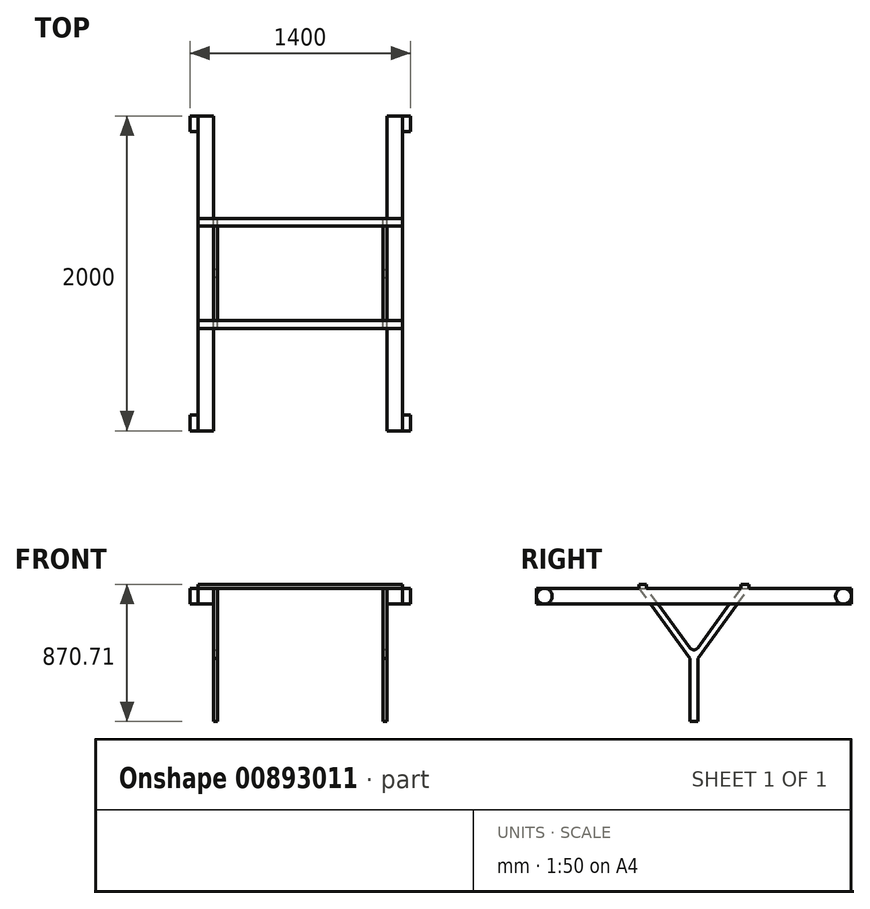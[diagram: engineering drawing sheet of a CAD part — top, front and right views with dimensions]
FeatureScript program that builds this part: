
annotation { "Feature Type Name" : "Feature", "Feature Type Description" : "" }
export const myFeature = defineFeature(function(context is Context, id is Id, definition is map)
    precondition{}
    {
        {
            var Q0;
            Q0=qCreatedBy(makeId("Top.planeOp"),FACE);
            var sketch = newSketch(context, id + "F0", { "sketchPlane" : qUnion([Q0])});
            skLineSegment(sketch, "E0.bottom", {"start": v(650, -1000) * mm, "end": v(550, -1000) * mm});
            skLineSegment(sketch, "E0.top", {"start": v(650, 1000) * mm, "end": v(550, 1000) * mm});
            skLineSegment(sketch, "E0.left", {"start": v(650, -1000) * mm, "end": v(650, 1000) * mm});
            skLineSegment(sketch, "E0.right", {"start": v(-650, -1000) * mm, "end": v(-650, 1000) * mm});
            skPoint(sketch, "E0.middle", {"position": v(0, 0) * mm});
            skLineSegment(sketch, "E1.left", {"start": v(-550, -1000) * mm, "end": v(-550, 1000) * mm});
            skLineSegment(sketch, "E1.right", {"start": v(550, -1000) * mm, "end": v(550, 1000) * mm});
            skLineSegment(sketch, "E2.trimOffspring", {"start": v(-550, 1000) * mm, "end": v(-650, 1000) * mm});
            skLineSegment(sketch, "E3.trimOffspring", {"start": v(-550, -1000) * mm, "end": v(-650, -1000) * mm});
            skSolve(sketch);
        }
        {
            var Q0;
            Q0=qSketchRegion(id+"F0",true);
            extrude(context, id + "F1", {"entities" : qUnion([Q0]), "depth" : 100 * mm, "offsetDistance" : 25 * mm});
        }
        {
            var Q0;
            Q0=makeQuery(id+"F1.opExtrude","CAP_FACE",FACE,{"disambiguationData":[OSD([sQuery(id+"F0.wireOp",EDGE,"E0.bottom"),sQuery(id+"F0.wireOp",EDGE,"E0.top"),sQuery(id+"F0.wireOp",EDGE,"E0.left"),sQuery(id+"F0.wireOp",EDGE,"E1.right")])],"isStart":false});
            var sketch = newSketch(context, id + "F2", { "sketchPlane" : qUnion([Q0])});
            skLineSegment(sketch, "E4.bottom", {"start": v(650, -350) * mm, "end": v(-650, -350) * mm});
            skLineSegment(sketch, "E4.top", {"start": v(650, -300) * mm, "end": v(-650, -300) * mm});
            skLineSegment(sketch, "E4.left", {"start": v(650, -350) * mm, "end": v(650, -300) * mm});
            skLineSegment(sketch, "E4.right", {"start": v(-650, -350) * mm, "end": v(-650, -300) * mm});
            skLineSegment(sketch, "E5.MirrorCS", {"start": v(-650, 350) * mm, "end": v(-650, 300) * mm});
            skLineSegment(sketch, "E6.MirrorCS", {"start": v(650, 350) * mm, "end": v(650, 300) * mm});
            skLineSegment(sketch, "E7.MirrorCS", {"start": v(650, 300) * mm, "end": v(-650, 300) * mm});
            skLineSegment(sketch, "E8.MirrorCS", {"start": v(650, 350) * mm, "end": v(-650, 350) * mm});
            skSolve(sketch);
        }
        {
            var Q0;
            Q0=qSketchRegion(id+"F2",true);
            extrude(context, id + "F3", {"entities" : qUnion([Q0]), "operationType" : NewBodyOperationType.ADD, "depth" : 25 * mm, "offsetDistance" : 25 * mm});
        }
        {
            var Q0;
            Q0=makeQuery(id+"F3.boolean.opBoolean","MERGE",FACE,{"derivedFrom":[makeQuery(id+"F1.opExtrude","SWEPT_FACE",FACE,{"disambiguationData":[OSD([sQuery(id+"F0.wireOp",EDGE,"E0.left")])]}),makeQuery(id+"F3.opExtrude","SWEPT_FACE",FACE,{"disambiguationData":[OSD([sQuery(id+"F2.wireOp",EDGE,"E4.left")])]}),makeQuery(id+"F3.opExtrude","SWEPT_FACE",FACE,{"disambiguationData":[OSD([sQuery(id+"F2.wireOp",EDGE,"E6.MirrorCS")])]})]});
            var sketch = newSketch(context, id + "F4", { "sketchPlane" : qUnion([Q0])});
            skCircle(sketch, "E9", {"center": v(-950, 50) * mm, "radius": 50 * mm});
            skCircle(sketch, "E10", {"center": v(950, 50) * mm, "radius": 50 * mm});
            skSolve(sketch);
        }
        {
            var Q0;
            Q0=qSketchRegion(id+"F4",true);
            extrude(context, id + "F5", {"entities" : qUnion([Q0]), "operationType" : NewBodyOperationType.ADD, "depth" : 50 * mm, "offsetDistance" : 25 * mm});
        }
        {
            var Q0;
            Q0=makeQuery(id+"F3.boolean.opBoolean","MERGE",FACE,{"derivedFrom":[makeQuery(id+"F1.opExtrude","SWEPT_FACE",FACE,{"disambiguationData":[OSD([sQuery(id+"F0.wireOp",EDGE,"E0.right")])]}),makeQuery(id+"F3.opExtrude","SWEPT_FACE",FACE,{"disambiguationData":[OSD([sQuery(id+"F2.wireOp",EDGE,"E4.right")])]}),makeQuery(id+"F3.opExtrude","SWEPT_FACE",FACE,{"disambiguationData":[OSD([sQuery(id+"F2.wireOp",EDGE,"E5.MirrorCS")])]})]});
            var sketch = newSketch(context, id + "F6", { "sketchPlane" : qUnion([Q0])});
            skCircle(sketch, "E11.0", {"center": v(-950, 50) * mm, "radius": 50 * mm});
            skCircle(sketch, "E12.0", {"center": v(950, 50) * mm, "radius": 50 * mm});
            skSolve(sketch);
        }
        {
            var Q0;
            Q0=qSketchRegion(id+"F6",true);
            extrude(context, id + "F7", {"entities" : qUnion([Q0]), "operationType" : NewBodyOperationType.ADD, "depth" : 50 * mm, "offsetDistance" : 25 * mm});
        }
        {
            var Q0;
            Q0=makeQuery(id+"F1.opExtrude","SWEPT_FACE",FACE,{"disambiguationData":[OSD([sQuery(id+"F0.wireOp",EDGE,"E1.left")])]});
            var sketch = newSketch(context, id + "F8", { "sketchPlane" : qUnion([Q0])});
            skLineSegment(sketch, "E13", {"start": v(-350, 100) * mm, "end": v(-25, -345.71) * mm});
            skLineSegment(sketch, "E14", {"start": v(25, -345.71) * mm, "end": v(350, 100) * mm});
            skLineSegment(sketch, "E15", {"start": v(350, 100) * mm, "end": v(300, 100) * mm});
            skLineSegment(sketch, "E16", {"start": v(300, 100) * mm, "end": v(0, -311.43) * mm});
            skLineSegment(sketch, "E17", {"start": v(0, -311.43) * mm, "end": v(-300, 100) * mm});
            skLineSegment(sketch, "E18", {"start": v(-300, 100) * mm, "end": v(-350, 100) * mm});
            skLineSegment(sketch, "E19.top", {"start": v(-25, -745.71) * mm, "end": v(25, -745.71) * mm});
            skLineSegment(sketch, "E19.left", {"start": v(-25, -345.71) * mm, "end": v(-25, -745.71) * mm});
            skLineSegment(sketch, "E19.right", {"start": v(25, -345.71) * mm, "end": v(25, -745.71) * mm});
            skPoint(sketch, "E20.orphan", {"position": v(0, -380) * mm});
            skSolve(sketch);
        }
        {
            var Q0;
            Q0=qSketchRegion(id+"F8",true);
            extrude(context, id + "F9", {"entities" : qUnion([Q0]), "operationType" : NewBodyOperationType.ADD, "depth" : 25 * mm, "offsetDistance" : 25 * mm});
        }
        {
            var Q0;
            Q0=makeQuery(id+"F1.opExtrude","SWEPT_FACE",FACE,{"disambiguationData":[OSD([sQuery(id+"F0.wireOp",EDGE,"E1.right")])]});
            var sketch = newSketch(context, id + "F10", { "sketchPlane" : qUnion([Q0])});
            skLineSegment(sketch, "E21.0.0", {"start": v(350, 100) * mm, "end": v(25, -345.71) * mm});
            skLineSegment(sketch, "E21.0.1", {"start": v(-25, -345.71) * mm, "end": v(-350, 100) * mm});
            skLineSegment(sketch, "E21.0.2", {"start": v(-350, 100) * mm, "end": v(-300, 100) * mm});
            skLineSegment(sketch, "E21.0.3", {"start": v(-300, 100) * mm, "end": v(0, -311.43) * mm});
            skLineSegment(sketch, "E21.0.4", {"start": v(0, -311.43) * mm, "end": v(300, 100) * mm});
            skLineSegment(sketch, "E21.0.5", {"start": v(300, 100) * mm, "end": v(350, 100) * mm});
            skLineSegment(sketch, "E22.0", {"start": v(25, -345.71) * mm, "end": v(25, -745.71) * mm});
            skLineSegment(sketch, "E23.0", {"start": v(-25, -345.71) * mm, "end": v(-25, -745.71) * mm});
            skPoint(sketch, "E24.0", {"position": v(0, -745.71) * mm});
            skLineSegment(sketch, "E25.0", {"start": v(25, -745.71) * mm, "end": v(-25, -745.71) * mm});
            skSolve(sketch);
        }
        {
            var Q0;
            Q0=qSketchRegion(id+"F10",true);
            extrude(context, id + "F11", {"entities" : qUnion([Q0]), "operationType" : NewBodyOperationType.ADD, "depth" : 25 * mm, "offsetDistance" : 25 * mm});
        }
        {
            var Q0;
            Q0=makeQuery(id+"F9.opExtrude","SWEPT_EDGE",EDGE,{"disambiguationData":[OSD([sQuery(id+"F8.wireOp",EDGE,"E16"),sQuery(id+"F8.wireOp",EDGE,"E17")])]});
            var Q1;
            Q1=makeQuery(id+"F11.opExtrude","SWEPT_EDGE",EDGE,{"disambiguationData":[OSD([sQuery(id+"F10.wireOp",EDGE,"E21.0.3"),sQuery(id+"F10.wireOp",EDGE,"E21.0.4")])]});
            fillet(context, id + "F12", {"entities" : qUnion([Q0, Q1]), "radius" : 30 * mm, "tangentPropagation" : true, "allowEdgeOverflow" : false});
        }
    });
